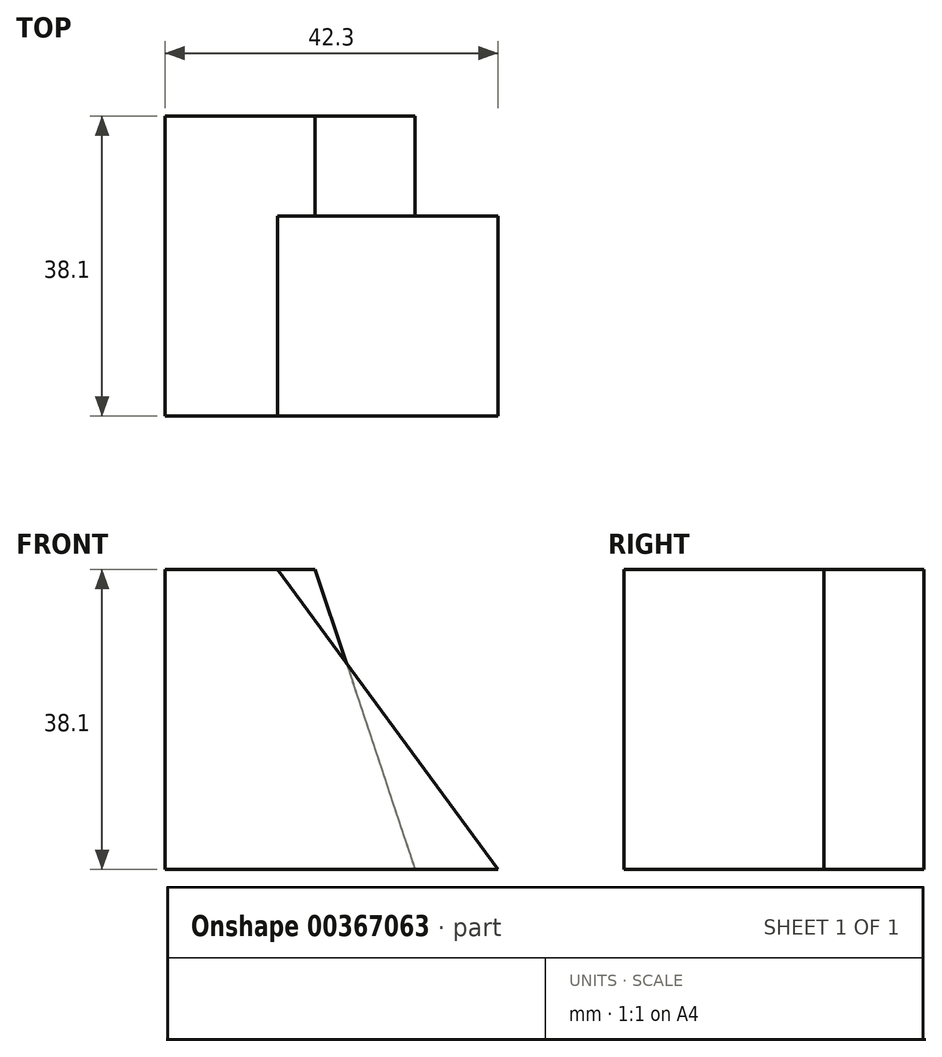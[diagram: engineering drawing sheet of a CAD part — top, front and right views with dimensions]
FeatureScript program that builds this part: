
annotation { "Feature Type Name" : "Feature", "Feature Type Description" : "" }
export const myFeature = defineFeature(function(context is Context, id is Id, definition is map)
    precondition{}
    {
        {
            var Q0;
            Q0=qCreatedBy(makeId("Front.planeOp"),FACE);
            var sketch = newSketch(context, id + "F0", { "sketchPlane" : qUnion([Q0])});
            skLineSegment(sketch, "E0", {"start": v(0, 0) * mm, "end": v(57.15, 0) * mm});
            skLineSegment(sketch, "E1", {"start": v(57.15, 0) * mm, "end": v(57.15, 38.1) * mm});
            skLineSegment(sketch, "E2", {"start": v(57.15, 38.1) * mm, "end": v(0, 38.1) * mm});
            skLineSegment(sketch, "E3", {"start": v(0, 38.1) * mm, "end": v(0, 0) * mm});
            skSolve(sketch);
        }
        {
            var Q0;
            Q0 = qSketchRegion(id + "F0", true);
            var Q1;
            Q1 = qSketchRegion(id + "F6", true);
            extrude(context, id + "F1", {"entities" : qUnion([Q0, Q1]), "depth" : 38.1 * mm});
        }
        {
            var Q0;
            Q0=makeQuery(id+"F1.opExtrude","CAP_FACE",FACE,{"disambiguationData":[OSD([sQuery(id+"F0.wireOp",EDGE,"E0"),sQuery(id+"F0.wireOp",EDGE,"E1"),sQuery(id+"F0.wireOp",EDGE,"E2"),sQuery(id+"F0.wireOp",EDGE,"E3")])],"isStart":false});
            var sketch = newSketch(context, id + "F2", { "sketchPlane" : qUnion([Q0])});
            skLineSegment(sketch, "E4", {"start": v(44.45, 38.1) * mm, "end": v(57.15, 0) * mm});
            skSolve(sketch);
        }
        {
            var Q0;
            Q0 = qSketchRegion(id + "F2", true);
            var Q1;
            {var subQ0=sQuery(id+"F2.wireOp",EDGE,"E4");Q1=makeQuery(id+"F2.imprint","IMPRINT",FACE,{"disambiguationData":[TD([[makeQuery(id+"F2.imprint","IMPRINT",EDGE,{"derivedFrom":subQ0}),1.0]])]});}
            extrude(context, id + "F3", {"entities" : qUnion([Q0, Q1]), "operationType" : NewBodyOperationType.REMOVE, "oppositeDirection" : true, "depth" : 38.1 * mm});
        }
        {
            var Q0;
            Q0=qCreatedBy(makeId("Front.planeOp"),FACE);
            var sketch = newSketch(context, id + "F4", { "sketchPlane" : qUnion([Q0])});
            skLineSegment(sketch, "E5", {"start": v(19.05, 38.2) * mm, "end": v(31.75, 0) * mm});
            skLineSegment(sketch, "E6", {"start": v(31.75, 0) * mm, "end": v(57.18, 0) * mm});
            skLineSegment(sketch, "E7", {"start": v(57.18, 0) * mm, "end": v(44.46, 38.26) * mm});
            skLineSegment(sketch, "E8", {"start": v(44.46, 38.26) * mm, "end": v(19.05, 38.2) * mm});
            skSolve(sketch);
        }
        {
            var Q0;
            Q0 = qSketchRegion(id + "F4", true);
            extrude(context, id + "F5", {"entities" : qUnion([Q0]), "operationType" : NewBodyOperationType.REMOVE, "depth" : 12.7 * mm});
        }
        {
            var Q0;
            Q0=qCreatedBy(makeId("Front.planeOp"),FACE);
            var sketch = newSketch(context, id + "F6", { "sketchPlane" : qUnion([Q0])});
            skLineSegment(sketch, "E9", {"start": v(14.94, 38.13) * mm, "end": v(42.99, 0) * mm});
            skSolve(sketch);
        }
        {
            var Q0;
            Q0=makeQuery(id+"F1.opExtrude","CAP_FACE",FACE,{"disambiguationData":[OSD([sQuery(id+"F0.wireOp",EDGE,"E0"),sQuery(id+"F0.wireOp",EDGE,"E1"),sQuery(id+"F0.wireOp",EDGE,"E2"),sQuery(id+"F0.wireOp",EDGE,"E3")])],"isStart":false});
            var sketch = newSketch(context, id + "F7", { "sketchPlane" : qUnion([Q0])});
            skLineSegment(sketch, "E10", {"start": v(14.26, 38.1) * mm, "end": v(42.3, 0) * mm});
            skLineSegment(sketch, "E11", {"start": v(14.26, 38.1) * mm, "end": v(44.45, 38.1) * mm});
            skLineSegment(sketch, "E12", {"start": v(44.45, 38.1) * mm, "end": v(57.15, 0) * mm});
            skLineSegment(sketch, "E13", {"start": v(57.15, 0) * mm, "end": v(42.3, 0) * mm});
            skSolve(sketch);
        }
        {
            var Q0;
            Q0 = qSketchRegion(id + "F7", true);
            extrude(context, id + "F8", {"entities" : qUnion([Q0]), "operationType" : NewBodyOperationType.REMOVE, "oppositeDirection" : true, "depth" : 25.4 * mm});
        }
        {
            var Q0;
            Q0 = qSketchRegion(id + "F7", true);
            extrude(context, id + "F9", {"entities" : qUnion([Q0]), "operationType" : NewBodyOperationType.REMOVE, "oppositeDirection" : true, "depth" : 12.7 * mm});
        }
    });
